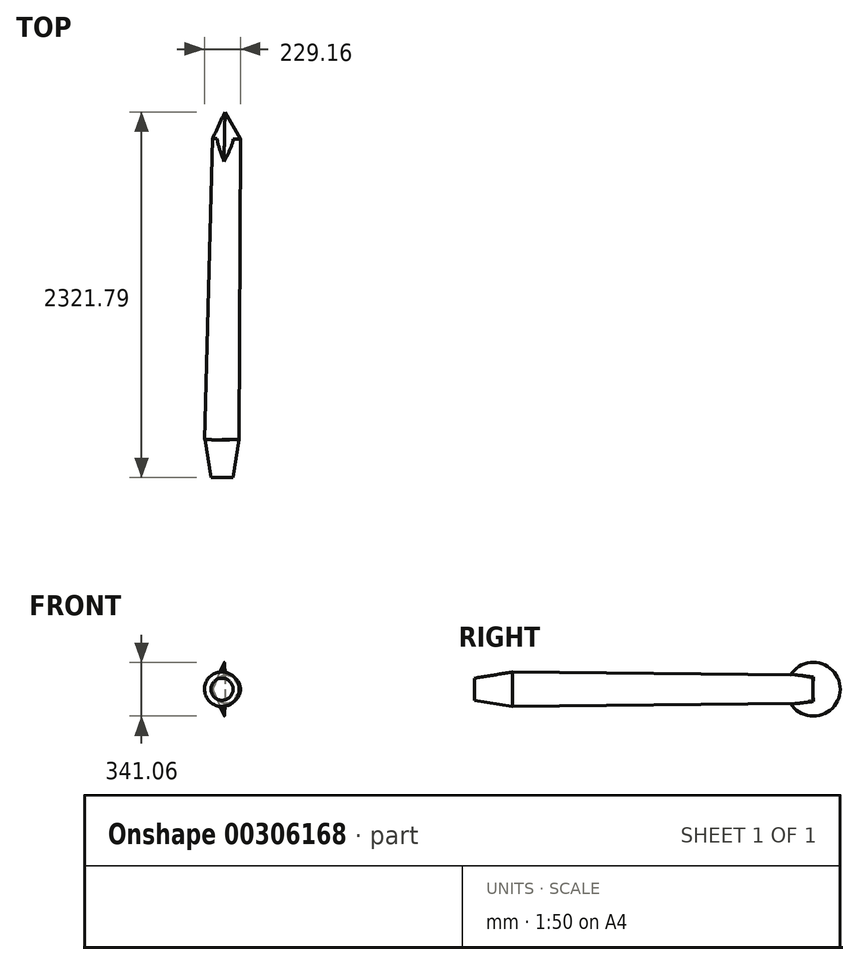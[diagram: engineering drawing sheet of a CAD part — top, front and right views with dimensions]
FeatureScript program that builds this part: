
annotation { "Feature Type Name" : "Feature", "Feature Type Description" : "" }
export const myFeature = defineFeature(function(context is Context, id is Id, definition is map)
    precondition{}
    {
        {
            var Q0;
            Q0=qCreatedBy(makeId("Top.planeOp"),FACE);
            var sketch = newSketch(context, id + "F0", { "sketchPlane" : qUnion([Q0])});
            skLineSegment(sketch, "E0", {"start": v(-29.01, 130.77) * mm, "end": v(-80.85, -1781.59) * mm});
            skLineSegment(sketch, "E1", {"start": v(-80.85, -1781.59) * mm, "end": v(28.5, -1784.55) * mm});
            skLineSegment(sketch, "E2", {"start": v(-29.01, 130.77) * mm, "end": v(59.63, 128.37) * mm});
            skLineSegment(sketch, "E3", {"start": v(59.63, 128.37) * mm, "end": v(28.5, -1784.55) * mm});
            skSolve(sketch);
        }
        {
            var Q0;
            Q0 = qSketchRegion(id + "F0", true);
            var Q1;
            Q1=sQuery(id+"F0.wireOp",EDGE,"E3");
            revolve(context, id + "F1", {"entities" : qUnion([Q0]), "axis" : qUnion([Q1]), "revolveType" : RevolveType.FULL});
        }
        {
            var Q0;
            Q0=qCreatedBy(makeId("Top.planeOp"),FACE);
            var sketch = newSketch(context, id + "F2", { "sketchPlane" : qUnion([Q0])});
            skLineSegment(sketch, "E4", {"start": v(-28.76, 130.98) * mm, "end": v(49.36, 300.15) * mm});
            skLineSegment(sketch, "E5", {"start": v(49.36, 300.15) * mm, "end": v(147.67, 127.83) * mm});
            skLineSegment(sketch, "E6", {"start": v(-28.76, 130.98) * mm, "end": v(147.67, 127.83) * mm});
            skSolve(sketch);
        }
        {
            var Q0;
            Q0 = qSketchRegion(id + "F2", true);
            var Q1;
            Q1=sQuery(id+"F2.wireOp",EDGE,"E6");
            revolve(context, id + "F3", {"operationType" : NewBodyOperationType.ADD, "entities" : qUnion([Q0]), "axis" : qUnion([Q1]), "revolveType" : RevolveType.FULL});
        }
        {
            var Q0;
            Q0=qCreatedBy(makeId("Top.planeOp"),FACE);
            var sketch = newSketch(context, id + "F4", { "sketchPlane" : qUnion([Q0])});
            skLineSegment(sketch, "E7", {"start": v(30.63, -1780.99) * mm, "end": v(30.63, -2021.64) * mm});
            skLineSegment(sketch, "E8", {"start": v(30.63, -2021.64) * mm, "end": v(-39.7, -2021.64) * mm});
            skLineSegment(sketch, "E9", {"start": v(-39.7, -2021.64) * mm, "end": v(-78.76, -1780.99) * mm});
            skLineSegment(sketch, "E10", {"start": v(-78.76, -1780.99) * mm, "end": v(30.63, -1780.99) * mm});
            skSolve(sketch);
        }
        {
            var Q0;
            Q0=makeQuery(id+"F4.imprint","IMPRINT",FACE,{"disambiguationData":[TD([[makeQuery(id+"F4.imprint","IMPRINT",EDGE,{"derivedFrom":sQuery(id+"F4.wireOp",EDGE,"E7")}),-1.0]])]});
            var Q1;
            Q1=sQuery(id+"F4.wireOp",EDGE,"E7");
            revolve(context, id + "F5", {"entities" : qUnion([Q0]), "axis" : qUnion([Q1]), "revolveType" : RevolveType.FULL});
        }
    });
